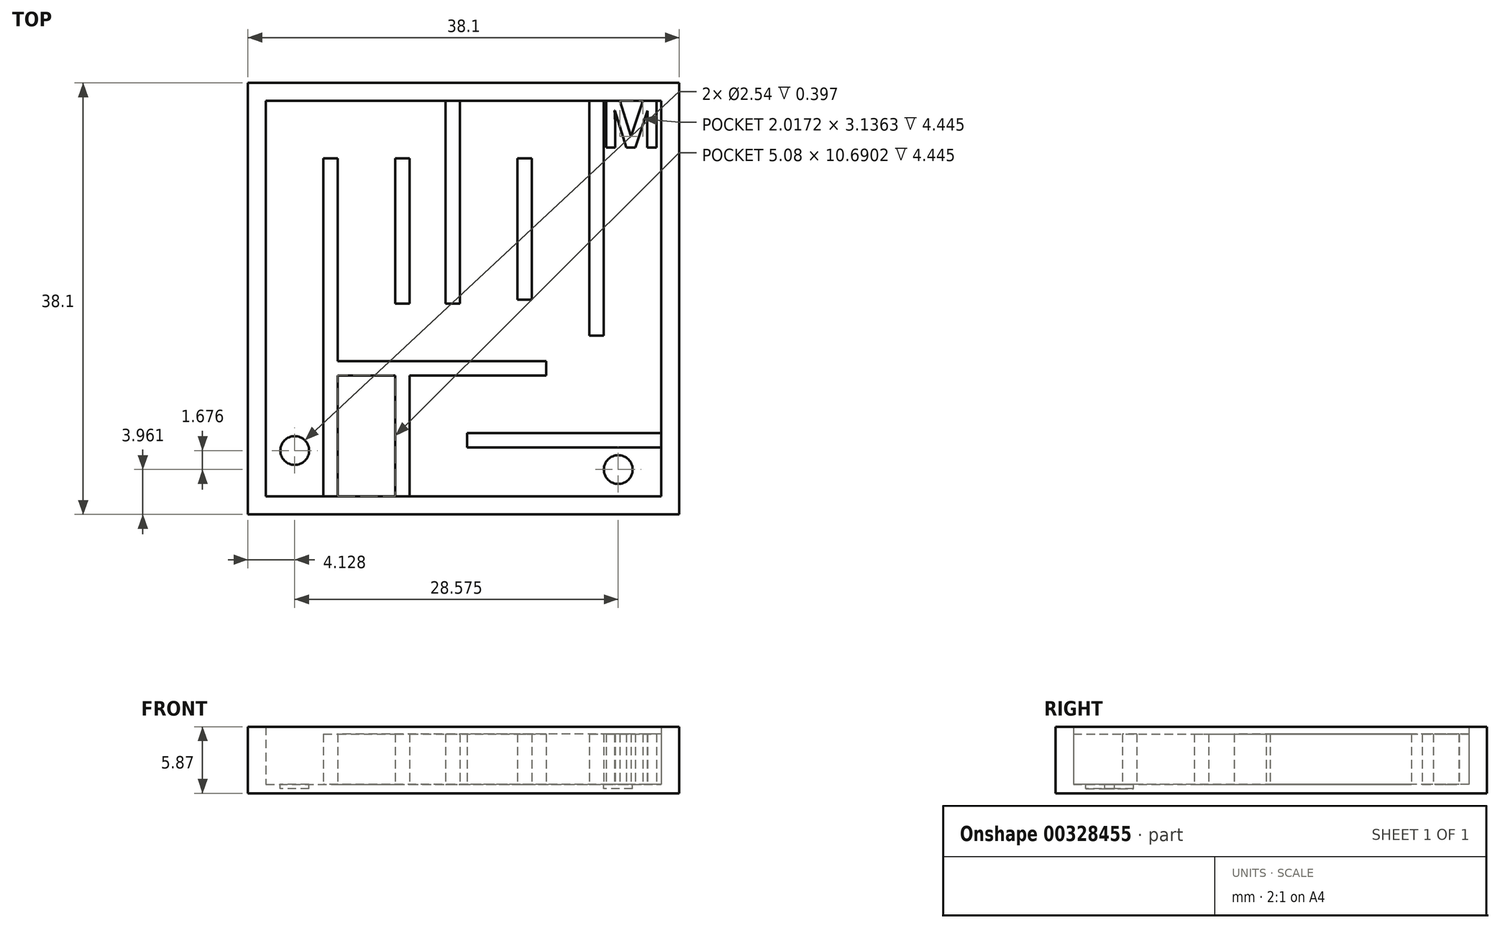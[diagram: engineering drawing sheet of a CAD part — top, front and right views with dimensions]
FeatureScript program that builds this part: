
annotation { "Feature Type Name" : "Feature", "Feature Type Description" : "" }
export const myFeature = defineFeature(function(context is Context, id is Id, definition is map)
    precondition{}
    {
        {
            var Q0;
            Q0=qCreatedBy(makeId("Top.planeOp"),FACE);
            var sketch = newSketch(context, id + "F0", { "sketchPlane" : qUnion([Q0])});
            skLineSegment(sketch, "E0.bottom", {"start": v(-20.39, 20.2) * mm, "end": v(17.71, 20.2) * mm});
            skLineSegment(sketch, "E0.top", {"start": v(-20.39, -17.9) * mm, "end": v(17.71, -17.9) * mm});
            skLineSegment(sketch, "E0.left", {"start": v(-20.39, 20.2) * mm, "end": v(-20.39, -17.9) * mm});
            skLineSegment(sketch, "E0.right", {"start": v(17.71, 20.2) * mm, "end": v(17.71, -17.9) * mm});
            skSolve(sketch);
        }
        {
            var Q0;
            Q0=makeQuery(id+"F0.imprint","IMPRINT",FACE,{"disambiguationData":[TD([[makeQuery(id+"F0.imprint","IMPRINT",EDGE,{"derivedFrom":sQuery(id+"F0.wireOp",EDGE,"E0.bottom")}),-1.0]])]});
            extrude(context, id + "F1", {"entities" : qUnion([Q0]), "depth" : 0.8 * mm});
        }
        {
            var Q0;
            Q0=makeQuery(id+"F1.opExtrude","CAP_FACE",FACE,{"disambiguationData":[OSD([sQuery(id+"F0.wireOp",EDGE,"E0.bottom"),sQuery(id+"F0.wireOp",EDGE,"E0.top"),sQuery(id+"F0.wireOp",EDGE,"E0.left"),sQuery(id+"F0.wireOp",EDGE,"E0.right")])],"isStart":false});
            var sketch = newSketch(context, id + "F2", { "sketchPlane" : qUnion([Q0])});
            skLineSegment(sketch, "E1.0", {"start": v(-18.8, 18.61) * mm, "end": v(16.12, 18.61) * mm});
            skLineSegment(sketch, "E1.1", {"start": v(-18.8, 18.61) * mm, "end": v(-18.8, -16.31) * mm});
            skLineSegment(sketch, "E1.2", {"start": v(-18.8, -16.31) * mm, "end": v(16.12, -16.31) * mm});
            skLineSegment(sketch, "E1.3", {"start": v(16.12, 18.61) * mm, "end": v(16.12, -16.31) * mm});
            skSolve(sketch);
        }
        {
            var Q0;
            Q0=makeQuery(id+"F2.imprint","IMPRINT",FACE,{"disambiguationData":[TD([[makeQuery(id+"F2.imprint","IMPRINT",EDGE,{"derivedFrom":sQuery(id+"F2.wireOp",EDGE,"E1.0")}),1.0]])]});
            extrude(context, id + "F3", {"entities" : qUnion([Q0]), "operationType" : NewBodyOperationType.ADD, "depth" : 5.08 * mm});
        }
        {
            var Q0;
            Q0=makeQuery(id+"F1.opExtrude","CAP_FACE",FACE,{"disambiguationData":[OSD([sQuery(id+"F0.wireOp",EDGE,"E0.bottom"),sQuery(id+"F0.wireOp",EDGE,"E0.top"),sQuery(id+"F0.wireOp",EDGE,"E0.left"),sQuery(id+"F0.wireOp",EDGE,"E0.right")])],"isStart":false});
            var sketch = newSketch(context, id + "F4", { "sketchPlane" : qUnion([Q0])});
            skLineSegment(sketch, "E2.bottom", {"start": v(-12.45, -16.31) * mm, "end": v(-13.72, -16.31) * mm});
            skLineSegment(sketch, "E2.top", {"start": v(-12.45, 13.53) * mm, "end": v(-13.72, 13.53) * mm});
            skLineSegment(sketch, "E2.left", {"start": v(-12.45, -16.31) * mm, "end": v(-12.45, -5.62) * mm});
            skLineSegment(sketch, "E2.right", {"start": v(-13.72, -16.31) * mm, "end": v(-13.72, 13.53) * mm});
            skLineSegment(sketch, "E3.bottom", {"start": v(-12.45, -5.62) * mm, "end": v(-7.37, -5.62) * mm});
            skLineSegment(sketch, "E3.right", {"start": v(5.96, -5.62) * mm, "end": v(5.96, -4.35) * mm});
            skLineSegment(sketch, "E4.trimOffspring", {"start": v(-12.45, -4.35) * mm, "end": v(-12.45, 13.53) * mm});
            skLineSegment(sketch, "E5.top", {"start": v(-7.37, 0.73) * mm, "end": v(-6.1, 0.73) * mm});
            skLineSegment(sketch, "E5.left", {"start": v(-7.37, 13.53) * mm, "end": v(-7.37, 0.73) * mm});
            skLineSegment(sketch, "E5.right", {"start": v(-6.1, 13.53) * mm, "end": v(-6.1, 0.73) * mm});
            skLineSegment(sketch, "E6.bottom", {"start": v(-2.93, 0.73) * mm, "end": v(-1.66, 0.73) * mm});
            skLineSegment(sketch, "E7.top", {"start": v(-7.37, -16.31) * mm, "end": v(-6.1, -16.31) * mm});
            skLineSegment(sketch, "E7.left", {"start": v(-7.37, -5.62) * mm, "end": v(-7.37, -16.31) * mm});
            skLineSegment(sketch, "E7.right", {"start": v(-6.1, -5.62) * mm, "end": v(-6.1, -16.31) * mm});
            skLineSegment(sketch, "E8.trimOffspring", {"start": v(-6.1, -5.62) * mm, "end": v(5.96, -5.62) * mm});
            skLineSegment(sketch, "E9", {"start": v(-7.37, 13.53) * mm, "end": v(-6.1, 13.53) * mm});
            skLineSegment(sketch, "E10", {"start": v(-2.93, 0.73) * mm, "end": v(-2.93, 18.61) * mm});
            skLineSegment(sketch, "E11", {"start": v(-2.93, 18.61) * mm, "end": v(-1.66, 18.61) * mm});
            skLineSegment(sketch, "E12", {"start": v(-1.66, 18.61) * mm, "end": v(-1.66, 0.73) * mm});
            skLineSegment(sketch, "E13", {"start": v(5.96, -4.35) * mm, "end": v(-12.45, -4.35) * mm});
            skLineSegment(sketch, "E14.bottom", {"start": v(3.42, 1.05) * mm, "end": v(4.7, 1.05) * mm});
            skLineSegment(sketch, "E14.top", {"start": v(3.42, 13.53) * mm, "end": v(4.7, 13.53) * mm});
            skLineSegment(sketch, "E14.left", {"start": v(3.42, 1.05) * mm, "end": v(3.42, 13.53) * mm});
            skLineSegment(sketch, "E14.right", {"start": v(4.7, 1.05) * mm, "end": v(4.7, 13.53) * mm});
            skLineSegment(sketch, "E15.bottom", {"start": v(9.77, 18.61) * mm, "end": v(11.04, 18.61) * mm});
            skLineSegment(sketch, "E15.top", {"start": v(9.77, -2.12) * mm, "end": v(11.04, -2.12) * mm});
            skLineSegment(sketch, "E15.left", {"start": v(9.77, 18.61) * mm, "end": v(9.77, -2.12) * mm});
            skLineSegment(sketch, "E15.right", {"start": v(11.04, 18.61) * mm, "end": v(11.04, -2.12) * mm});
            skLineSegment(sketch, "E16.bottom", {"start": v(16.12, -10.7) * mm, "end": v(-1.02, -10.7) * mm});
            skLineSegment(sketch, "E16.top", {"start": v(16.12, -11.97) * mm, "end": v(-1.02, -11.97) * mm});
            skLineSegment(sketch, "E16.left", {"start": v(16.12, -10.7) * mm, "end": v(16.12, -11.97) * mm});
            skLineSegment(sketch, "E16.right", {"start": v(-1.02, -10.7) * mm, "end": v(-1.02, -11.97) * mm});
            skLineSegment(sketch, "E17", {"start": v(-18.8, -16.31) * mm, "end": v(-13.72, -16.31) * mm});
            skCircle(sketch, "E18", {"center": v(-16.26, -12.26) * mm, "radius": 1.27 * mm});
            skPoint(sketch, "E18.centerSnap0", {"position": v(-16.26, -16.31) * mm});
            skLineSegment(sketch, "E19", {"start": v(8.5, -16.31) * mm, "end": v(16.12, -16.31) * mm});
            skCircle(sketch, "E20", {"center": v(12.31, -13.94) * mm, "radius": 1.27 * mm});
            skPoint(sketch, "E20.centerSnap0", {"position": v(12.31, -16.31) * mm});
            skText(sketch, "E21", { "text": "M", "fontName": "OpenSans-Bold.ttf"});
            const initialGuessF4  = {"E21": [0.01074, 0.0145, 1, 0, 0.00418]};
            skSetInitialGuess(sketch, initialGuessF4);
            skSolve(sketch);
        }
        {
            var Q0;
            Q0=makeQuery(id+"F4.imprint","IMPRINT",FACE,{"disambiguationData":[TD([[makeQuery(id+"F4.imprint","IMPRINT",EDGE,{"derivedFrom":sQuery(id+"F4.wireOp",EDGE,"E2.bottom")}),1.0]])]});
            var Q1;
            Q1=makeQuery(id+"F4.imprint","IMPRINT",FACE,{"disambiguationData":[TD([[makeQuery(id+"F4.imprint","IMPRINT",EDGE,{"derivedFrom":sQuery(id+"F4.wireOp",EDGE,"E5.top")}),1.0]])]});
            var Q2;
            Q2=makeQuery(id+"F4.imprint","IMPRINT",FACE,{"disambiguationData":[TD([[makeQuery(id+"F4.imprint","IMPRINT",EDGE,{"derivedFrom":sQuery(id+"F4.wireOp",EDGE,"E6.bottom")}),1.0]])]});
            var Q3;
            Q3=makeQuery(id+"F4.imprint","IMPRINT",FACE,{"disambiguationData":[TD([[makeQuery(id+"F4.imprint","IMPRINT",EDGE,{"derivedFrom":sQuery(id+"F4.wireOp",EDGE,"E14.bottom")}),1.0]])]});
            var Q4;
            Q4=makeQuery(id+"F4.imprint","IMPRINT",FACE,{"disambiguationData":[TD([[makeQuery(id+"F4.imprint","IMPRINT",EDGE,{"derivedFrom":sQuery(id+"F4.wireOp",EDGE,"E15.bottom")}),-1.0]])]});
            var Q5;
            Q5=makeQuery(id+"F4.imprint","IMPRINT",FACE,{"disambiguationData":[TD([[makeQuery(id+"F4.imprint","IMPRINT",EDGE,{"derivedFrom":sQuery(id+"F4.wireOp",EDGE,"E16.bottom")}),1.0]])]});
            extrude(context, id + "F5", {"entities" : qUnion([Q0, Q1, Q2, Q3, Q4, Q5]), "operationType" : NewBodyOperationType.ADD, "depth" : 4.44 * mm});
        }
        {
            var Q0;
            Q0=makeQuery(id+"F4.imprint","IMPRINT",FACE,{"disambiguationData":[TD([[makeQuery(id+"F4.imprint","IMPRINT",EDGE,{"derivedFrom":sQuery(id+"F4.wireOp",EDGE,"E21.sketch_text.stroke-0")}),-1.0]])]});
            extrude(context, id + "F6", {"entities" : qUnion([Q0]), "operationType" : NewBodyOperationType.ADD, "depth" : 4.44 * mm});
        }
        {
            var Q0;
            Q0=makeQuery(id+"F4.imprint","IMPRINT",FACE,{"disambiguationData":[TD([[makeQuery(id+"F4.imprint","IMPRINT",EDGE,{"derivedFrom":sQuery(id+"F4.wireOp",EDGE,"E18")}),1.0]])]});
            var Q1;
            Q1=makeQuery(id+"F4.imprint","IMPRINT",FACE,{"disambiguationData":[TD([[makeQuery(id+"F4.imprint","IMPRINT",EDGE,{"derivedFrom":sQuery(id+"F4.wireOp",EDGE,"E20")}),1.0]])]});
            extrude(context, id + "F7", {"entities" : qUnion([Q0, Q1]), "operationType" : NewBodyOperationType.REMOVE, "oppositeDirection" : true, "depth" : 0.4 * mm});
        }
    });
